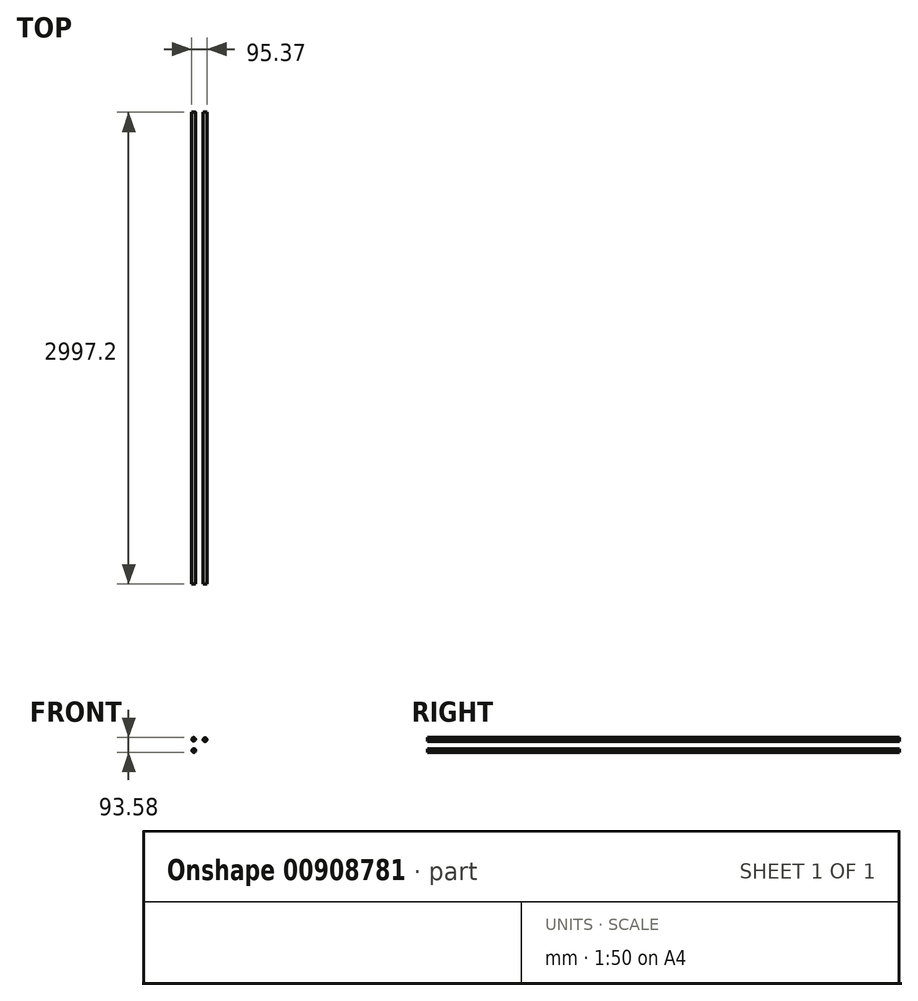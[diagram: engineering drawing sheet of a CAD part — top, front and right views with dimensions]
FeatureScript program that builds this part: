
annotation { "Feature Type Name" : "Feature", "Feature Type Description" : "" }
export const myFeature = defineFeature(function(context is Context, id is Id, definition is map)
    precondition{}
    {
        {
            var Q0;
            Q0=qCreatedBy(makeId("Front.planeOp"),FACE);
            var sketch = newSketch(context, id + "F0", { "sketchPlane" : qUnion([Q0])});
            skCircle(sketch, "E0", {"center": v(-53.7, 27.52) * mm, "radius": 11.43 * mm});
            skCircle(sketch, "E1", {"center": v(-61.82, -40.76) * mm, "radius": 12.29 * mm});
            skCircle(sketch, "E2", {"center": v(35.04, 27.52) * mm, "radius": 11.18 * mm});
            skSolve(sketch);
        }
        {
            var Q0;
            Q0=makeQuery(id+"F0.imprint","IMPRINT",FACE,{"disambiguationData":[TD([[makeQuery(id+"F0.imprint","IMPRINT",EDGE,{"derivedFrom":sQuery(id+"F0.wireOp",EDGE,"E0")}),1.0]])]});
            extrude(context, id + "F1", {"entities" : qUnion([Q0]), "depth" : 2997.2 * mm, "offsetDistance" : 25.4 * mm});
        }
        {
            var Q0;
            Q0=qCreatedBy(makeId("Front.planeOp"),FACE);
            var sketch = newSketch(context, id + "F2", { "sketchPlane" : qUnion([Q0])});
            skCircle(sketch, "E3", {"center": v(-51.89, -36.55) * mm, "radius": 11.45 * mm});
            skCircle(sketch, "E4", {"center": v(18.8, 25.12) * mm, "radius": 11.45 * mm});
            skSolve(sketch);
        }
        {
            var Q0;
            Q0=makeQuery(id+"F2.imprint","IMPRINT",FACE,{"disambiguationData":[TD([[makeQuery(id+"F2.imprint","IMPRINT",EDGE,{"derivedFrom":sQuery(id+"F2.wireOp",EDGE,"E4")}),1.0]])]});
            extrude(context, id + "F3", {"entities" : qUnion([Q0]), "depth" : 2997.2 * mm, "offsetDistance" : 25.4 * mm});
        }
        {
            var Q0;
            Q0=qCreatedBy(makeId("Front.planeOp"),FACE);
            var sketch = newSketch(context, id + "F4", { "sketchPlane" : qUnion([Q0])});
            skCircle(sketch, "E5", {"center": v(-51.59, -43.16) * mm, "radius": 11.45 * mm});
            skSolve(sketch);
        }
        {
            var Q0;
            Q0=makeQuery(id+"F4.imprint","IMPRINT",FACE,{"disambiguationData":[TD([[makeQuery(id+"F4.imprint","IMPRINT",EDGE,{"derivedFrom":sQuery(id+"F4.wireOp",EDGE,"E5")}),1.0]])]});
            extrude(context, id + "F5", {"entities" : qUnion([Q0]), "depth" : 2997.2 * mm, "offsetDistance" : 25.4 * mm});
        }
    });
